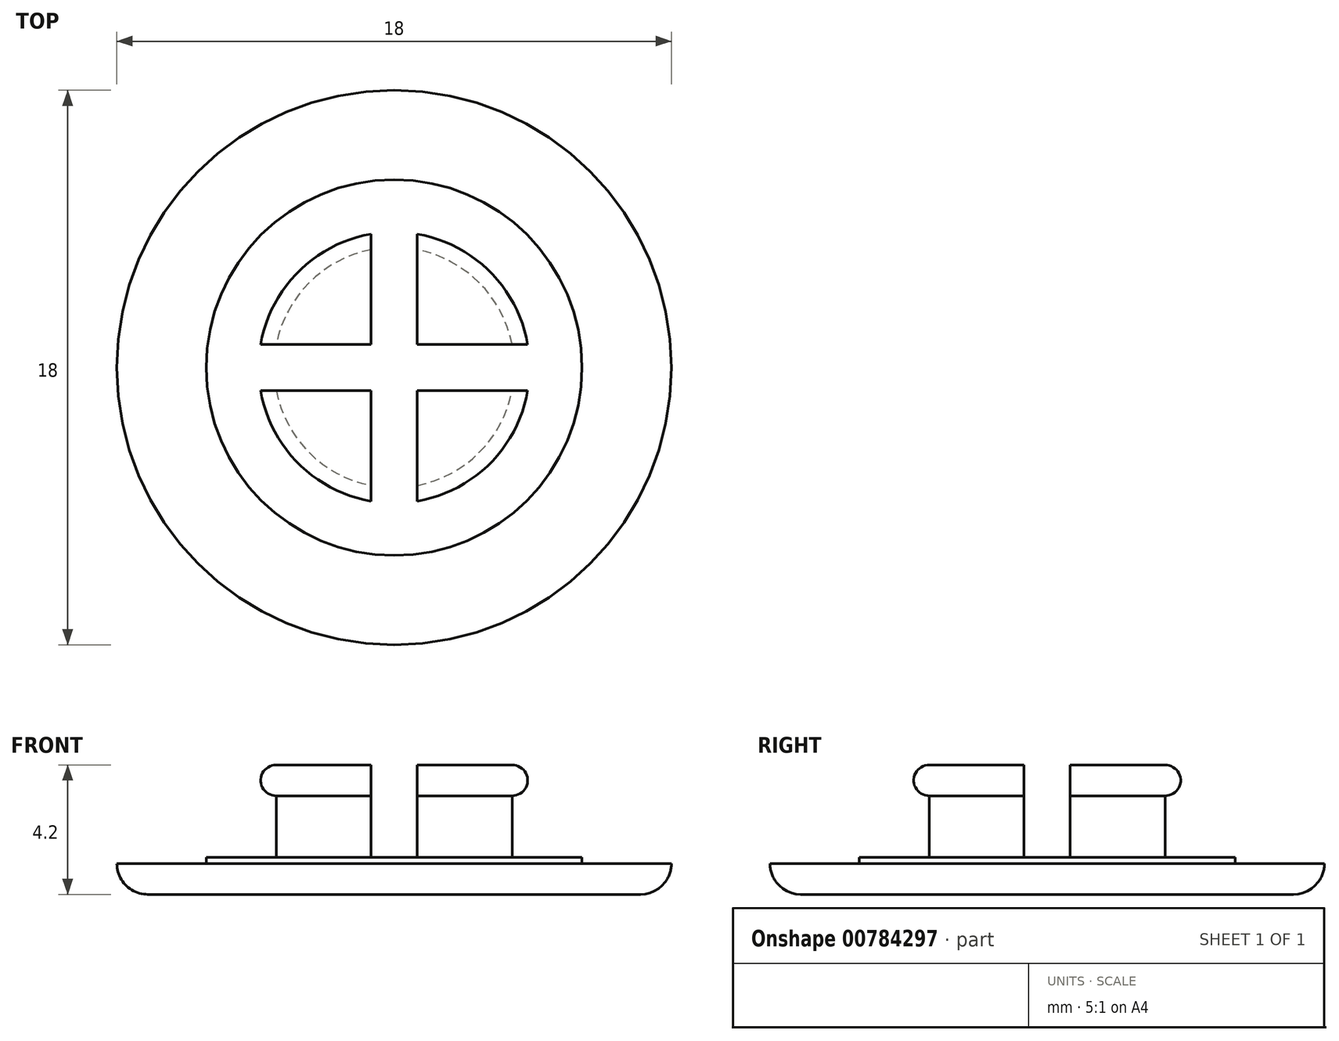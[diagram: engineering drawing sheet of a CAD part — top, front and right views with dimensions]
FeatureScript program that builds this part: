
annotation { "Feature Type Name" : "Feature", "Feature Type Description" : "" }
export const myFeature = defineFeature(function(context is Context, id is Id, definition is map)
    precondition{}
    {
        {
            var Q0;
            Q0=qCreatedBy(makeId("Front.planeOp"),FACE);
            var sketch = newSketch(context, id + "F0", { "sketchPlane" : qUnion([Q0])});
            skLineSegment(sketch, "E0.bottom", {"start": v(0, 0) * mm, "end": v(9, 0) * mm});
            skLineSegment(sketch, "E0.top", {"start": v(6.1, 1) * mm, "end": v(9, 1) * mm});
            skLineSegment(sketch, "E0.left", {"start": v(0, 0) * mm, "end": v(0, 1) * mm});
            skLineSegment(sketch, "E0.right", {"start": v(9, 0) * mm, "end": v(9, 1) * mm});
            skLineSegment(sketch, "E1.top", {"start": v(3.9, 1.2) * mm, "end": v(6.1, 1.2) * mm});
            skLineSegment(sketch, "E1.left", {"start": v(0, 1) * mm, "end": v(0, 1.2) * mm});
            skLineSegment(sketch, "E1.right", {"start": v(6.1, 1) * mm, "end": v(6.1, 1.2) * mm});
            skLineSegment(sketch, "E2.top", {"start": v(0, 4.2) * mm, "end": v(3.9, 4.2) * mm});
            skLineSegment(sketch, "E2.left", {"start": v(0, 1.2) * mm, "end": v(0, 4.2) * mm});
            skLineSegment(sketch, "E2.right", {"start": v(3.9, 1.2) * mm, "end": v(3.9, 3.2) * mm});
            skArc(sketch, "E3", {"start": v(3.9, 3.2) * mm, "mid": v(4.4, 3.7) * mm, "end": v(3.9, 4.2) * mm});
            skSolve(sketch);
        }
        {
            var Q0;
            Q0=makeQuery(id+"F0.imprint","IMPRINT",FACE,{"disambiguationData":[TD([[makeQuery(id+"F0.imprint","IMPRINT",EDGE,{"derivedFrom":sQuery(id+"F0.wireOp",EDGE,"E0.bottom")}),1.0]])]});
            var Q1;
            Q1=sQuery(id+"F0.wireOp",EDGE,"E2.left");
            revolve(context, id + "F1", {"surfaceOperationType" : NewSurfaceOperationType.NEW, "entities" : qUnion([Q0]), "axis" : qUnion([Q1]), "revolveType" : RevolveType.FULL});
        }
        {
            var Q0;
            Q0=makeQuery(id+"F1.opRevolve","SWEPT_EDGE",EDGE,{"disambiguationData":[OSD([sQuery(id+"F0.wireOp",EDGE,"E0.bottom"),sQuery(id+"F0.wireOp",EDGE,"E0.right")])]});
            fillet(context, id + "F2", {"entities" : qUnion([Q0]), "radius" : 1 * mm, "tangentPropagation" : true, "allowEdgeOverflow" : false});
        }
        {
            var Q0;
            Q0=makeQuery(id+"F1.opRevolve","SWEPT_FACE",FACE,{"disambiguationData":[OSD([sQuery(id+"F0.wireOp",EDGE,"E2.top")])]});
            var sketch = newSketch(context, id + "F3", { "sketchPlane" : qUnion([Q0])});
            skLineSegment(sketch, "E4.bottom", {"start": v(5.25, 0.75) * mm, "end": v(0.75, 0.75) * mm});
            skLineSegment(sketch, "E4.top", {"start": v(5.25, -0.75) * mm, "end": v(0.75, -0.75) * mm});
            skLineSegment(sketch, "E4.left", {"start": v(5.25, 0.75) * mm, "end": v(5.25, -0.75) * mm});
            skLineSegment(sketch, "E4.right", {"start": v(-5.25, 0.75) * mm, "end": v(-5.25, -0.75) * mm});
            skPoint(sketch, "E4.middle", {"position": v(0, 0) * mm});
            skLineSegment(sketch, "E5.bottom", {"start": v(-0.75, 5.25) * mm, "end": v(0.75, 5.25) * mm});
            skLineSegment(sketch, "E5.top", {"start": v(-0.75, -5.25) * mm, "end": v(0.75, -5.25) * mm});
            skLineSegment(sketch, "E5.left", {"start": v(-0.75, 5.25) * mm, "end": v(-0.75, 0.75) * mm});
            skLineSegment(sketch, "E5.right", {"start": v(0.75, 5.25) * mm, "end": v(0.75, 0.75) * mm});
            skLineSegment(sketch, "E6.trimOffspring", {"start": v(-0.75, 0.75) * mm, "end": v(-5.25, 0.75) * mm});
            skLineSegment(sketch, "E7.trimOffspring", {"start": v(-0.75, -0.75) * mm, "end": v(-0.75, -5.25) * mm});
            skLineSegment(sketch, "E8.trimOffspring", {"start": v(0.75, -0.75) * mm, "end": v(0.75, -5.25) * mm});
            skLineSegment(sketch, "E9.trimOffspring", {"start": v(-0.75, -0.75) * mm, "end": v(-5.25, -0.75) * mm});
            skSolve(sketch);
        }
        {
            var Q0;
            {var subQ0=sQuery(id+"F3.wireOp",EDGE,"E4.bottom");var subQ5=sQuery(id+"F3.wireOp",EDGE,"E5.right");var subQ6=makeQuery(id+"F3.imprint","INTERSECT",VERTEX,{"derivedFrom":[subQ0,subQ5]});Q0=makeQuery(id+"F3.imprint","IMPRINT",FACE,{"disambiguationData":[TD([[makeQuery(id+"F3.imprint","IMPRINT",EDGE,{"disambiguationData":[TD([[subQ6,1.0]])],"derivedFrom":subQ0}),1.0]])]});}
            var Q1;
            {var subQ0=sQuery(id+"F3.wireOp",EDGE,"E4.right");Q1=makeQuery(id+"F3.imprint","IMPRINT",FACE,{"disambiguationData":[TD([[makeQuery(id+"F3.imprint","IMPRINT",EDGE,{"derivedFrom":subQ0}),1.0]])]});}
            var Q2;
            {var subQ0=sQuery(id+"F3.wireOp",EDGE,"E5.bottom");Q2=makeQuery(id+"F3.imprint","IMPRINT",FACE,{"disambiguationData":[TD([[makeQuery(id+"F3.imprint","IMPRINT",EDGE,{"derivedFrom":subQ0}),-1.0]])]});}
            var Q3;
            {var subQ0=sQuery(id+"F3.wireOp",EDGE,"E4.left");Q3=makeQuery(id+"F3.imprint","IMPRINT",FACE,{"disambiguationData":[TD([[makeQuery(id+"F3.imprint","IMPRINT",EDGE,{"derivedFrom":subQ0}),-1.0]])]});}
            var Q4;
            {var subQ0=sQuery(id+"F3.wireOp",EDGE,"E5.top");Q4=makeQuery(id+"F3.imprint","IMPRINT",FACE,{"disambiguationData":[TD([[makeQuery(id+"F3.imprint","IMPRINT",EDGE,{"derivedFrom":subQ0}),1.0]])]});}
            extrude(context, id + "F4", {"entities" : qUnion([Q0, Q1, Q2, Q3, Q4]), "operationType" : NewBodyOperationType.REMOVE, "oppositeDirection" : true, "depth" : 3 * mm, "offsetDistance" : 25 * mm});
        }
    });
